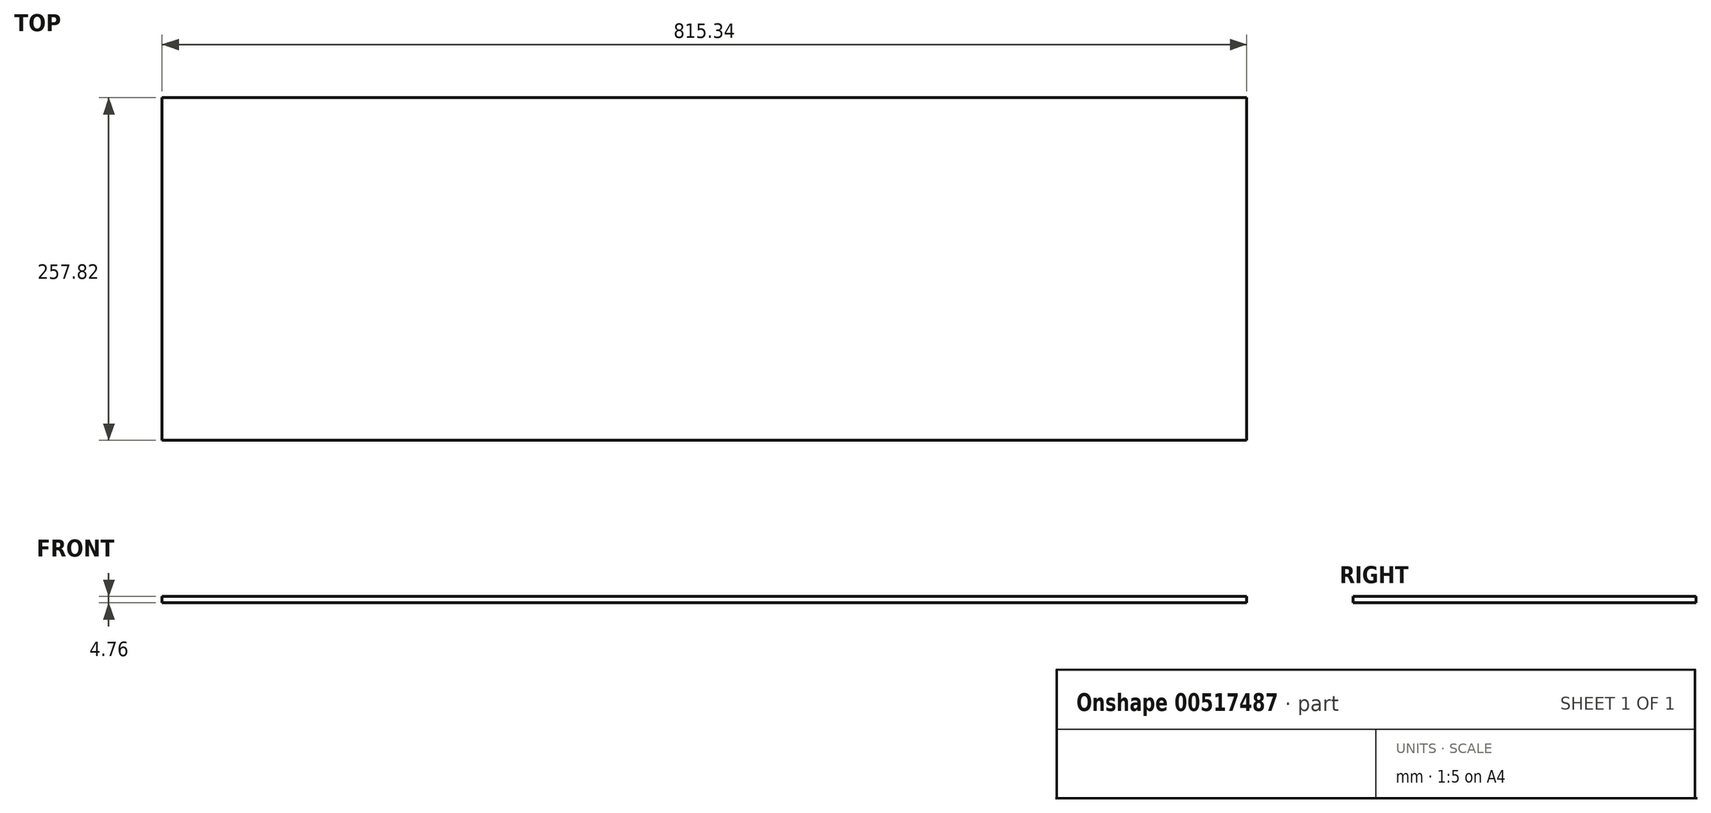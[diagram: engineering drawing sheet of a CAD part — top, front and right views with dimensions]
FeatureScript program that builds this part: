
annotation { "Feature Type Name" : "Feature", "Feature Type Description" : "" }
export const myFeature = defineFeature(function(context is Context, id is Id, definition is map)
    precondition{}
    {
        {
            var Q0;
            Q0=qCreatedBy(makeId("Top.planeOp"),FACE);
            var sketch = newSketch(context, id + "F0", { "sketchPlane" : qUnion([Q0])});
            skLineSegment(sketch, "E0.bottom", {"start": v(407.67, -128.9) * mm, "end": v(-407.67, -128.9) * mm});
            skLineSegment(sketch, "E0.top", {"start": v(407.67, 128.9) * mm, "end": v(-407.67, 128.9) * mm});
            skLineSegment(sketch, "E0.left", {"start": v(407.67, -128.9) * mm, "end": v(407.67, 128.9) * mm});
            skLineSegment(sketch, "E0.right", {"start": v(-407.67, -128.9) * mm, "end": v(-407.67, 128.9) * mm});
            skPoint(sketch, "E0.middle", {"position": v(0, 0) * mm});
            skLineSegment(sketch, "E1", {"start": v(407.67, 128.9) * mm, "end": v(163.83, 128.9) * mm});
            skLineSegment(sketch, "E2", {"start": v(-407.67, -128.9) * mm, "end": v(-245.11, -128.9) * mm});
            skLineSegment(sketch, "E3", {"start": v(-245.11, -128.9) * mm, "end": v(-245.11, -433.7) * mm});
            skLineSegment(sketch, "E4", {"start": v(-245.11, -433.7) * mm, "end": v(-407.67, -433.7) * mm});
            skLineSegment(sketch, "E5", {"start": v(-407.67, -128.9) * mm, "end": v(-407.67, -433.7) * mm});
            skLineSegment(sketch, "E6.bottom", {"start": v(163.83, 128.9) * mm, "end": v(407.67, 128.9) * mm});
            skLineSegment(sketch, "E6.top", {"start": v(163.83, 281.3) * mm, "end": v(407.67, 281.3) * mm});
            skLineSegment(sketch, "E6.left", {"start": v(163.83, 128.9) * mm, "end": v(163.83, 281.3) * mm});
            skLineSegment(sketch, "E6.right", {"start": v(407.67, 128.9) * mm, "end": v(407.67, 281.3) * mm});
            skSolve(sketch);
        }
        {
            var Q0;
            Q0=makeQuery(id+"F0.imprint","IMPRINT",FACE,{"disambiguationData":[TD([[makeQuery(id+"F0.imprint","IMPRINT",EDGE,{"derivedFrom":sQuery(id+"F0.wireOp",EDGE,"E0.bottom")}),-1.0]])]});
            var Q1;
            Q1=makeQuery(id+"F0.imprint","IMPRINT",FACE,{"disambiguationData":[TD([[makeQuery(id+"F0.imprint","IMPRINT",EDGE,{"derivedFrom":sQuery(id+"F0.wireOp",EDGE,"E6.bottom")}),1.0]])]});
            extrude(context, id + "F1", {"entities" : qUnion([Q0, Q1]), "depth" : 4.76 * mm, "offsetDistance" : 25.4 * mm});
        }
    });
